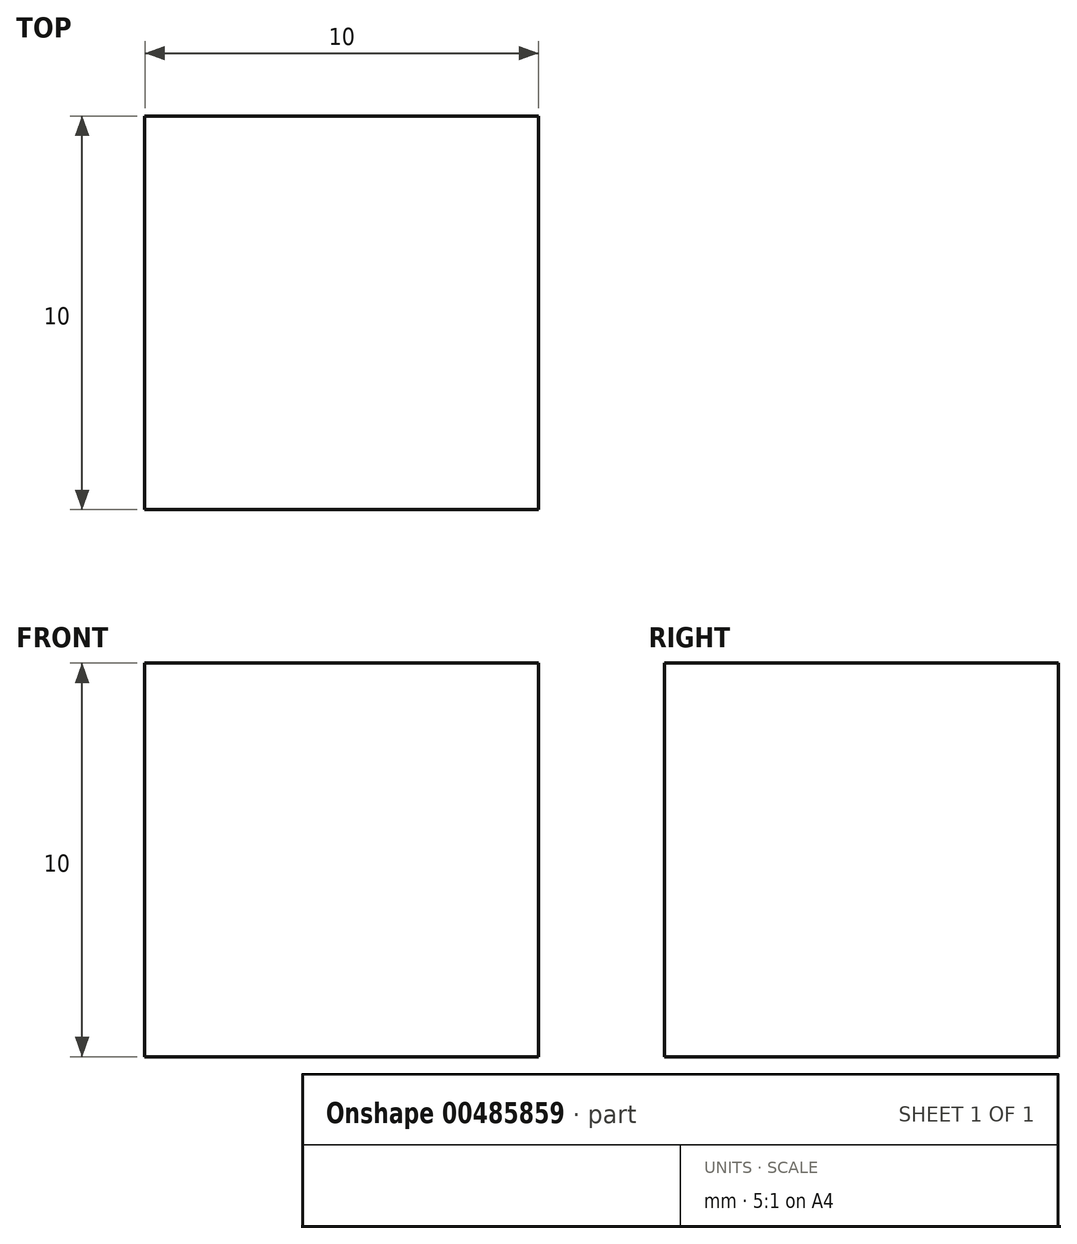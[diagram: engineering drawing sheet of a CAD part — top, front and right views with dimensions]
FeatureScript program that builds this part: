
annotation { "Feature Type Name" : "Feature", "Feature Type Description" : "" }
export const myFeature = defineFeature(function(context is Context, id is Id, definition is map)
    precondition{}
    {
        {
            var Q0;
            Q0=qCreatedBy(makeId("Top.planeOp"),FACE);
            var sketch = newSketch(context, id + "F0", { "sketchPlane" : qUnion([Q0])});
            skLineSegment(sketch, "E0.bottom", {"start": v(-6, 7.14) * mm, "end": v(4, 7.14) * mm});
            skLineSegment(sketch, "E0.top", {"start": v(-6, -2.86) * mm, "end": v(4, -2.86) * mm});
            skLineSegment(sketch, "E0.left", {"start": v(-6, 7.14) * mm, "end": v(-6, -2.86) * mm});
            skLineSegment(sketch, "E0.right", {"start": v(4, 7.14) * mm, "end": v(4, -2.86) * mm});
            skSolve(sketch);
        }
        {
            var Q0;
            Q0=makeQuery(id+"F0.imprint","IMPRINT",FACE,{"disambiguationData":[TD([[makeQuery(id+"F0.imprint","IMPRINT",EDGE,{"derivedFrom":sQuery(id+"F0.wireOp",EDGE,"E0.bottom")}),-1.0]])]});
            extrude(context, id + "F1", {"entities" : qUnion([Q0]), "depth" : 10 * mm});
        }
    });
